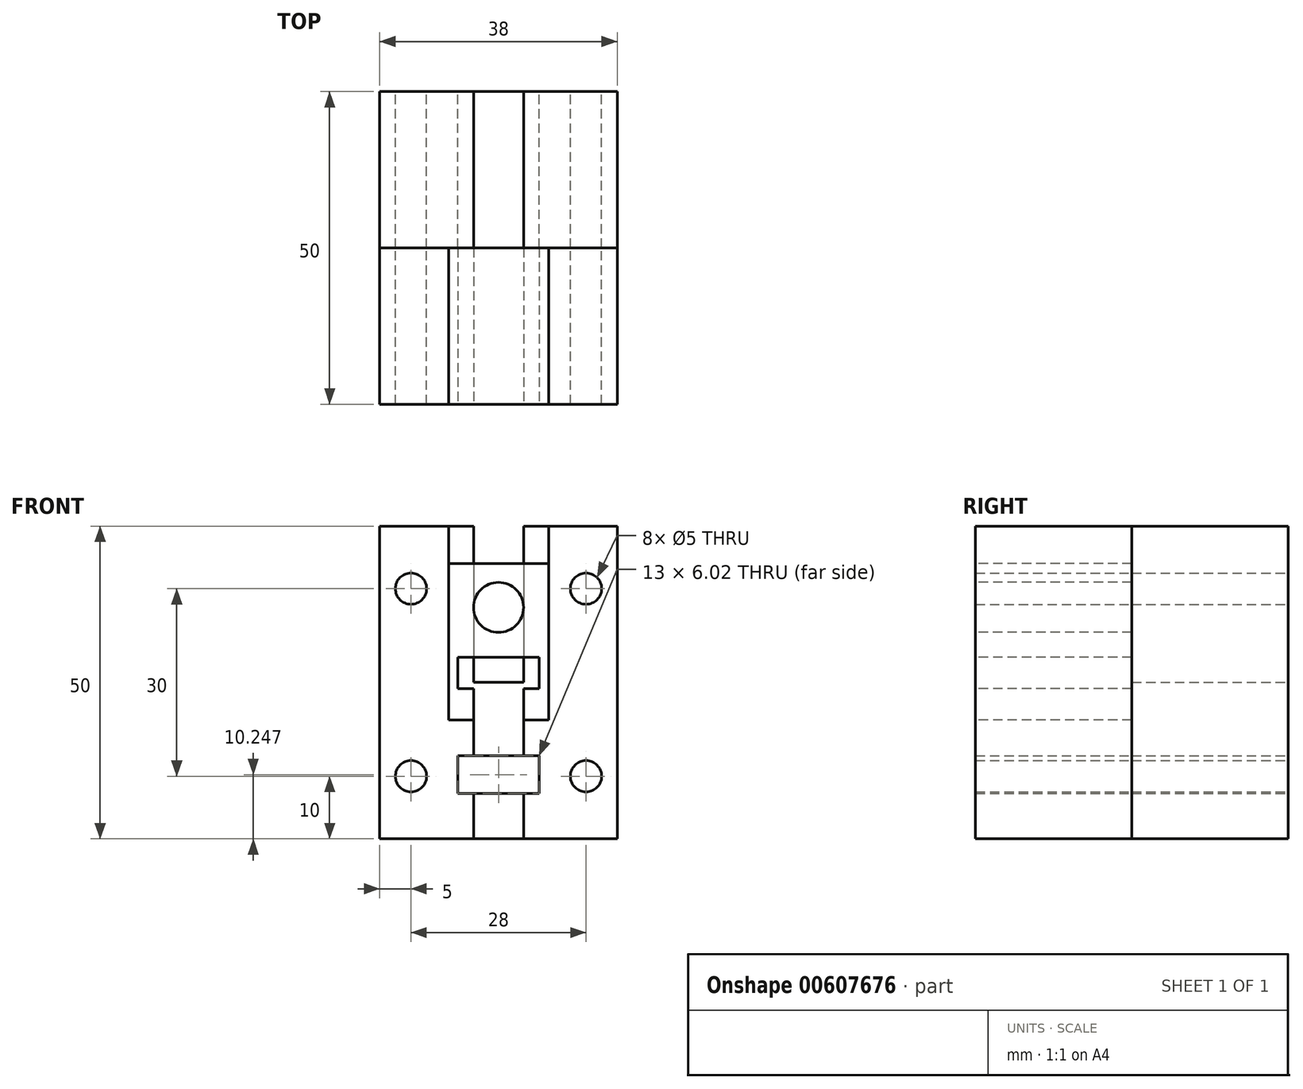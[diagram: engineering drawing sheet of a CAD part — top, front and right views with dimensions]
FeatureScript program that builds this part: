
annotation { "Feature Type Name" : "Feature", "Feature Type Description" : "" }
export const myFeature = defineFeature(function(context is Context, id is Id, definition is map)
    precondition{}
    {
        {
            var Q0;
            Q0=qCreatedBy(makeId("Front.planeOp"),FACE);
            var sketch = newSketch(context, id + "F0", { "sketchPlane" : qUnion([Q0])});
            skLineSegment(sketch, "E0.bottom", {"start": v(0, 0) * mm, "end": v(38, 0) * mm});
            skLineSegment(sketch, "E0.top", {"start": v(0, 50) * mm, "end": v(15, 50) * mm});
            skLineSegment(sketch, "E0.left", {"start": v(0, 0) * mm, "end": v(0, 50) * mm});
            skLineSegment(sketch, "E0.right", {"start": v(38, 0) * mm, "end": v(38, 50) * mm});
            skLineSegment(sketch, "E1.top", {"start": v(15, 25) * mm, "end": v(23, 25) * mm});
            skLineSegment(sketch, "E1.left", {"start": v(15, 50) * mm, "end": v(15, 25) * mm});
            skLineSegment(sketch, "E1.right", {"start": v(23, 50) * mm, "end": v(23, 25) * mm});
            skLineSegment(sketch, "E2.trimOffspring", {"start": v(23, 50) * mm, "end": v(38, 50) * mm});
            skCircle(sketch, "E3", {"center": v(5, 40) * mm, "radius": 2.5 * mm});
            skCircle(sketch, "E4", {"center": v(5, 10) * mm, "radius": 2.5 * mm});
            skCircle(sketch, "E5", {"center": v(33, 10) * mm, "radius": 2.5 * mm});
            skCircle(sketch, "E6", {"center": v(33, 40) * mm, "radius": 2.5 * mm});
            skLineSegment(sketch, "E7.bottom", {"start": v(12.5, 13.26) * mm, "end": v(25.5, 13.26) * mm});
            skLineSegment(sketch, "E7.top", {"start": v(12.5, 7.24) * mm, "end": v(25.5, 7.24) * mm});
            skLineSegment(sketch, "E7.left", {"start": v(12.5, 13.26) * mm, "end": v(12.5, 7.24) * mm});
            skLineSegment(sketch, "E7.right", {"start": v(25.5, 13.26) * mm, "end": v(25.5, 7.24) * mm});
            skSolve(sketch);
        }
        {
            var Q0;
            Q0 = qSketchRegion(id + "F0", true);
            extrude(context, id + "F1", {"entities" : qUnion([Q0]), "depth" : 25 * mm, "offsetDistance" : 25 * mm});
        }
        {
            var Q0;
            Q0=makeQuery(id+"F1.opExtrude","CAP_FACE",FACE,{"disambiguationData":[OSD([sQuery(id+"F0.wireOp",EDGE,"E0.bottom"),sQuery(id+"F0.wireOp",EDGE,"E0.top"),sQuery(id+"F0.wireOp",EDGE,"E0.left"),sQuery(id+"F0.wireOp",EDGE,"E0.right"),sQuery(id+"F0.wireOp",EDGE,"E1.top"),sQuery(id+"F0.wireOp",EDGE,"E1.left"),sQuery(id+"F0.wireOp",EDGE,"E1.right"),sQuery(id+"F0.wireOp",EDGE,"E2.trimOffspring"),sQuery(id+"F0.wireOp",EDGE,"E3"),sQuery(id+"F0.wireOp",EDGE,"E4"),sQuery(id+"F0.wireOp",EDGE,"E5"),sQuery(id+"F0.wireOp",EDGE,"E6")])],"isStart":false});
            var sketch = newSketch(context, id + "F2", { "sketchPlane" : qUnion([Q0])});
            skLineSegment(sketch, "E8.0.2", {"start": v(11, 50) * mm, "end": v(0, 50) * mm});
            skLineSegment(sketch, "E8.0.3", {"start": v(0, 50) * mm, "end": v(0, 0) * mm});
            skLineSegment(sketch, "E8.0.4", {"start": v(0, 0) * mm, "end": v(11, 0) * mm});
            skLineSegment(sketch, "E8.0.5", {"start": v(38, 0) * mm, "end": v(38, 50) * mm});
            skLineSegment(sketch, "E8.0.6", {"start": v(38, 50) * mm, "end": v(27, 50) * mm});
            skCircle(sketch, "E9.0", {"center": v(5, 40) * mm, "radius": 2.5 * mm});
            skCircle(sketch, "E10.0", {"center": v(5, 10) * mm, "radius": 2.5 * mm});
            skCircle(sketch, "E11.0", {"center": v(33, 10) * mm, "radius": 2.5 * mm});
            skCircle(sketch, "E12.0", {"center": v(33, 40) * mm, "radius": 2.5 * mm});
            skLineSegment(sketch, "E13.left", {"start": v(11, 50) * mm, "end": v(11, 19) * mm});
            skLineSegment(sketch, "E13.right", {"start": v(27, 50) * mm, "end": v(27, 19) * mm});
            skPoint(sketch, "E13.bottom.end.orphan", {"position": v(15, 50) * mm});
            skPoint(sketch, "E14.trimOffspring.start.orphan", {"position": v(23, 50) * mm});
            skPoint(sketch, "E8.0.0.end.orphan", {"position": v(15, 25) * mm});
            skPoint(sketch, "E8.0.0.start.orphan", {"position": v(23, 25) * mm});
            skLineSegment(sketch, "E15.trimOffspring", {"start": v(27, 0) * mm, "end": v(38, 0) * mm});
            skLineSegment(sketch, "E16.bottom", {"start": v(11, 19) * mm, "end": v(15, 19) * mm});
            skLineSegment(sketch, "E16.top", {"start": v(11, 0) * mm, "end": v(15, 0) * mm});
            skLineSegment(sketch, "E17.left", {"start": v(15, 19) * mm, "end": v(15, 13.26) * mm});
            skLineSegment(sketch, "E18.0", {"start": v(12.5, 13.26) * mm, "end": v(15, 13.26) * mm});
            skLineSegment(sketch, "E19.0", {"start": v(12.5, 13.26) * mm, "end": v(12.5, 7.24) * mm});
            skLineSegment(sketch, "E20.0.4", {"start": v(0, 0) * mm, "end": v(15, 0) * mm});
            skLineSegment(sketch, "E21.0", {"start": v(12.5, 7.24) * mm, "end": v(15, 7.24) * mm});
            skPoint(sketch, "E22.0", {"position": v(25.5, 10.25) * mm});
            skLineSegment(sketch, "E23.0", {"start": v(25.5, 13.26) * mm, "end": v(25.5, 7.24) * mm});
            skLineSegment(sketch, "E24.trimOffspring", {"start": v(23, 19) * mm, "end": v(27, 19) * mm});
            skLineSegment(sketch, "E25.trimOffspring", {"start": v(23, 13.26) * mm, "end": v(25.5, 13.26) * mm});
            skLineSegment(sketch, "E26.trimOffspring", {"start": v(23, 7.24) * mm, "end": v(25.5, 7.24) * mm});
            skLineSegment(sketch, "E27.trimOffspring", {"start": v(15, 7.24) * mm, "end": v(15, 0) * mm});
            skLineSegment(sketch, "E28.trimOffspring", {"start": v(23, 7.24) * mm, "end": v(23, 0) * mm});
            skLineSegment(sketch, "E29", {"start": v(23, 13.26) * mm, "end": v(23, 19) * mm});
            skLineSegment(sketch, "E30.trimOffspring", {"start": v(23, 0) * mm, "end": v(38, 0) * mm});
            skLineSegment(sketch, "E31.trimOffspring", {"start": v(23, 0) * mm, "end": v(27, 0) * mm});
            skSolve(sketch);
        }
        {
            var Q0;
            Q0 = qSketchRegion(id + "F2", true);
            extrude(context, id + "F3", {"entities" : qUnion([Q0]), "depth" : 25 * mm, "offsetDistance" : 25 * mm});
        }
        {
            var Q0;
            Q0=makeQuery(id+"F3.opExtrude","CAP_FACE",FACE,{"disambiguationData":[OSD([sQuery(id+"F2.wireOp",EDGE,"E11.0"),sQuery(id+"F2.wireOp",EDGE,"E12.0"),sQuery(id+"F2.wireOp",EDGE,"E13.right"),sQuery(id+"F2.wireOp",EDGE,"E8.0.5"),sQuery(id+"F2.wireOp",EDGE,"E8.0.6"),sQuery(id+"F2.wireOp",EDGE,"E23.0"),sQuery(id+"F2.wireOp",EDGE,"E24.trimOffspring"),sQuery(id+"F2.wireOp",EDGE,"E25.trimOffspring"),sQuery(id+"F2.wireOp",EDGE,"E26.trimOffspring"),sQuery(id+"F2.wireOp",EDGE,"E28.trimOffspring"),sQuery(id+"F2.wireOp",EDGE,"E29"),sQuery(id+"F2.wireOp",EDGE,"E30.trimOffspring"),sQuery(id+"F2.wireOp",EDGE,"E31.trimOffspring")])],"isStart":false});
            var sketch = newSketch(context, id + "F4", { "sketchPlane" : qUnion([Q0])});
            skLineSegment(sketch, "E32.bottom", {"start": v(27, 19) * mm, "end": v(23, 19) * mm});
            skLineSegment(sketch, "E32.top", {"start": v(27, 44) * mm, "end": v(11, 44) * mm});
            skLineSegment(sketch, "E32.left", {"start": v(27, 19) * mm, "end": v(27, 44) * mm});
            skLineSegment(sketch, "E32.right", {"start": v(11, 19) * mm, "end": v(11, 44) * mm});
            skLineSegment(sketch, "E33.bottom", {"start": v(12.5, 29) * mm, "end": v(25.5, 29) * mm});
            skLineSegment(sketch, "E33.top", {"start": v(12.5, 24) * mm, "end": v(15, 24) * mm});
            skLineSegment(sketch, "E33.left", {"start": v(12.5, 29) * mm, "end": v(12.5, 24) * mm});
            skLineSegment(sketch, "E33.right", {"start": v(25.5, 29) * mm, "end": v(25.5, 24) * mm});
            skCircle(sketch, "E34", {"center": v(19, 37) * mm, "radius": 4 * mm});
            skPoint(sketch, "E34.centerSnap0", {"position": v(19, 44) * mm});
            skLineSegment(sketch, "E35.left", {"start": v(15, 24) * mm, "end": v(15, 19) * mm});
            skLineSegment(sketch, "E35.right", {"start": v(23, 24) * mm, "end": v(23, 19) * mm});
            skLineSegment(sketch, "E36.trimOffspring", {"start": v(23, 24) * mm, "end": v(25.5, 24) * mm});
            skLineSegment(sketch, "E37.trimOffspring", {"start": v(15, 19) * mm, "end": v(11, 19) * mm});
            skSolve(sketch);
        }
        {
            var Q0;
            Q0 = qSketchRegion(id + "F4", true);
            extrude(context, id + "F5", {"entities" : qUnion([Q0]), "oppositeDirection" : true, "depth" : 25 * mm, "offsetDistance" : 25 * mm});
        }
    });
